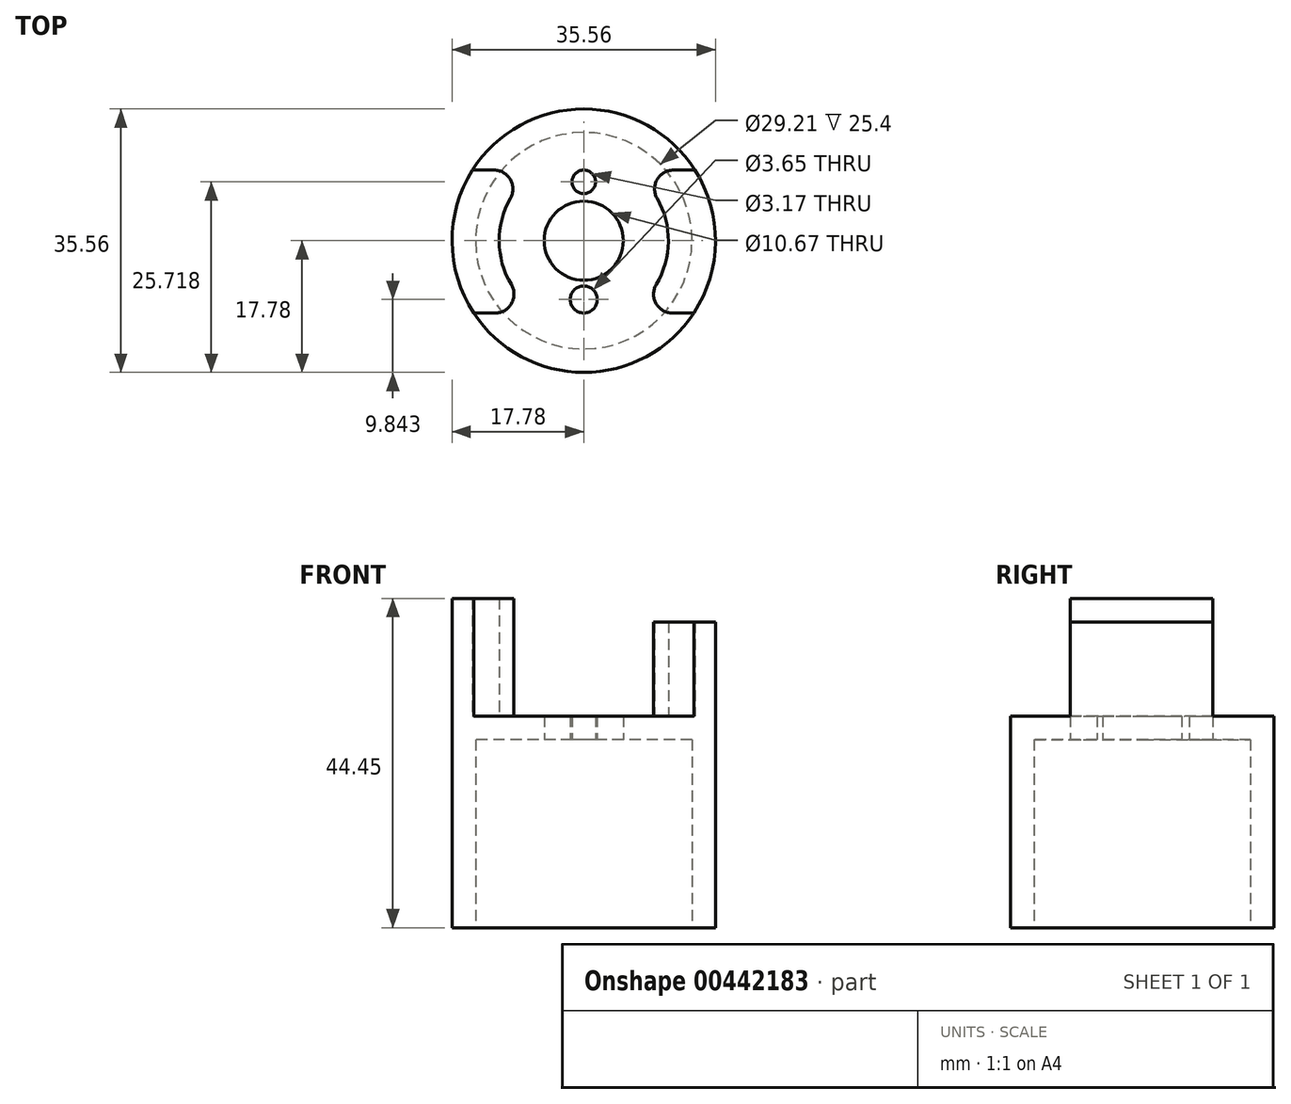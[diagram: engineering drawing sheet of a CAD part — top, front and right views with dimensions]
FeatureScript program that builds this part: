
annotation { "Feature Type Name" : "Feature", "Feature Type Description" : "" }
export const myFeature = defineFeature(function(context is Context, id is Id, definition is map)
    precondition{}
    {
        {
            var Q0;
            Q0=qCreatedBy(makeId("Top.planeOp"),FACE);
            var sketch = newSketch(context, id + "F0", { "sketchPlane" : qUnion([Q0])});
            skCircle(sketch, "E0", {"center": v(0, 0) * mm, "radius": 14.6 * mm});
            skCircle(sketch, "E1.0", {"center": v(0, 0) * mm, "radius": 17.78 * mm});
            skSolve(sketch);
        }
        {
            var Q0;
            Q0=makeQuery(id+"F0.imprint","IMPRINT",FACE,{"disambiguationData":[TD([[makeQuery(id+"F0.imprint","IMPRINT",EDGE,{"derivedFrom":sQuery(id+"F0.wireOp",EDGE,"E0")}),-1.0]])]});
            extrude(context, id + "F1", {"entities" : qUnion([Q0]), "depth" : 25.4 * mm});
        }
        {
            var Q0;
            Q0=makeQuery(id+"F1.opExtrude","CAP_FACE",FACE,{"disambiguationData":[OSD([sQuery(id+"F0.wireOp",EDGE,"E0"),sQuery(id+"F0.wireOp",EDGE,"E1.0")])],"isStart":false});
            var sketch = newSketch(context, id + "F2", { "sketchPlane" : qUnion([Q0])});
            skCircle(sketch, "E2", {"center": v(0, 0) * mm, "radius": 17.78 * mm});
            skCircle(sketch, "E3", {"center": v(0, 0) * mm, "radius": 7.94 * mm, "construction": true});
            skPoint(sketch, "E4", {"position": v(0, 7.94) * mm});
            skPoint(sketch, "E5", {"position": v(0, -7.94) * mm});
            skCircle(sketch, "E6", {"center": v(0, 7.94) * mm, "radius": 1.59 * mm});
            skCircle(sketch, "E7", {"center": v(0, -7.94) * mm, "radius": 1.82 * mm});
            skCircle(sketch, "E8", {"center": v(0, 0) * mm, "radius": 5.33 * mm});
            skSolve(sketch);
        }
        {
            var Q0;
            Q0 = qSketchRegion(id + "F2", true);
            extrude(context, id + "F3", {"entities" : qUnion([Q0]), "operationType" : NewBodyOperationType.ADD, "depth" : 3.17 * mm});
        }
        {
            var Q0;
            Q0=makeQuery(id+"F3.opExtrude","CAP_FACE",FACE,{"disambiguationData":[OSD([sQuery(id+"F2.wireOp",EDGE,"E2"),sQuery(id+"F2.wireOp",EDGE,"E6"),sQuery(id+"F2.wireOp",EDGE,"E7"),sQuery(id+"F2.wireOp",EDGE,"E8")])],"isStart":false});
            var sketch = newSketch(context, id + "F4", { "sketchPlane" : qUnion([Q0])});
            skLineSegment(sketch, "E9", {"start": v(-15.01, 9.53) * mm, "end": v(15.01, 9.53) * mm});
            skLineSegment(sketch, "E10", {"start": v(-14.86, -9.76) * mm, "end": v(14.86, -9.76) * mm});
            skArc(sketch, "E11", {"start": v(-15.01, 9.52) * mm, "mid": v(-17.78, -0.14) * mm, "end": v(-14.86, -9.76) * mm});
            skArc(sketch, "E12", {"start": v(14.86, -9.76) * mm, "mid": v(17.78, -0.14) * mm, "end": v(15.01, 9.52) * mm});
            skArc(sketch, "E13", {"start": v(-6.32, 9.52) * mm, "mid": v(-11.43, -0.22) * mm, "end": v(-5.95, -9.76) * mm});
            skArc(sketch, "E14", {"start": v(6.32, 9.52) * mm, "mid": v(11.43, -0.22) * mm, "end": v(5.95, -9.76) * mm});
            skSolve(sketch);
        }
        {
            var Q0;
            {var subQ0=sQuery(id+"F4.wireOp",EDGE,"E11");Q0=makeQuery(id+"F4.imprint","IMPRINT",FACE,{"disambiguationData":[TD([[makeQuery(id+"F4.imprint","IMPRINT",EDGE,{"derivedFrom":subQ0}),1.0]])]});}
            var Q1;
            {var subQ0=sQuery(id+"F4.wireOp",EDGE,"E12");Q1=makeQuery(id+"F4.imprint","IMPRINT",FACE,{"disambiguationData":[TD([[makeQuery(id+"F4.imprint","IMPRINT",EDGE,{"derivedFrom":subQ0}),1.0]])]});}
            extrude(context, id + "F5", {"entities" : qUnion([Q0, Q1]), "operationType" : NewBodyOperationType.ADD, "depth" : 12.7 * mm});
        }
        {
            var Q0;
            Q0=makeQuery(id+"F5.opExtrude","CAP_FACE",FACE,{"disambiguationData":[OSD([sQuery(id+"F4.wireOp",EDGE,"E9"),sQuery(id+"F4.wireOp",EDGE,"E10"),sQuery(id+"F4.wireOp",EDGE,"E11"),sQuery(id+"F4.wireOp",EDGE,"E13")])],"isStart":false});
            var sketch = newSketch(context, id + "F6", { "sketchPlane" : qUnion([Q0])});
            skLineSegment(sketch, "E15", {"start": v(0, 18.78) * mm, "end": v(0, -22.03) * mm, "construction": true});
            skArc(sketch, "E16", {"start": v(-15.01, 9.52) * mm, "mid": v(-17.78, -0.14) * mm, "end": v(-14.86, -9.76) * mm});
            skArc(sketch, "E17.MirrorCS", {"start": v(15.01, 9.52) * mm, "mid": v(17.78, -0.14) * mm, "end": v(14.86, -9.76) * mm});
            skLineSegment(sketch, "E18", {"start": v(-15.01, 9.52) * mm, "end": v(15.01, 9.52) * mm});
            skLineSegment(sketch, "E19", {"start": v(-14.86, -9.76) * mm, "end": v(14.86, -9.76) * mm});
            skCircle(sketch, "E20", {"center": v(0, 0) * mm, "radius": 7.5 * mm});
            skSolve(sketch);
        }
        {
            var Q0;
            {var subQ0=sQuery(id+"F6.wireOp",EDGE,"E16");Q0=makeQuery(id+"F6.imprint","IMPRINT",FACE,{"disambiguationData":[TD([[makeQuery(id+"F6.imprint","IMPRINT",EDGE,{"derivedFrom":subQ0}),1.0]])]});}
            var Q1;
            {var subQ0=sQuery(id+"F6.wireOp",EDGE,"E17.MirrorCS");Q1=makeQuery(id+"F6.imprint","IMPRINT",FACE,{"disambiguationData":[TD([[makeQuery(id+"F6.imprint","IMPRINT",EDGE,{"derivedFrom":subQ0}),-1.0]])]});}
            extrude(context, id + "F7", {"entities" : qUnion([Q0, Q1]), "operationType" : NewBodyOperationType.ADD, "depth" : 3.17 * mm});
        }
        {
            var Q0;
            Q0=makeQuery(id+"F5.opExtrude","SWEPT_EDGE",EDGE,{"disambiguationData":[OSD([sQuery(id+"F4.wireOp",EDGE,"E10"),sQuery(id+"F4.wireOp",EDGE,"E13")])]});
            var Q1;
            Q1=makeQuery(id+"F5.opExtrude","SWEPT_EDGE",EDGE,{"disambiguationData":[OSD([sQuery(id+"F4.wireOp",EDGE,"E10"),sQuery(id+"F4.wireOp",EDGE,"E14")])]});
            var Q2;
            Q2=makeQuery(id+"F5.opExtrude","SWEPT_EDGE",EDGE,{"disambiguationData":[OSD([sQuery(id+"F4.wireOp",EDGE,"E9"),sQuery(id+"F4.wireOp",EDGE,"E13")])]});
            var Q3;
            Q3=makeQuery(id+"F5.opExtrude","SWEPT_EDGE",EDGE,{"disambiguationData":[OSD([sQuery(id+"F4.wireOp",EDGE,"E9"),sQuery(id+"F4.wireOp",EDGE,"E14")])]});
            fillet(context, id + "F8", {"entities" : qUnion([Q0, Q1, Q2, Q3]), "radius" : 2.54 * mm, "tangentPropagation" : true, "allowEdgeOverflow" : false});
        }
    });
